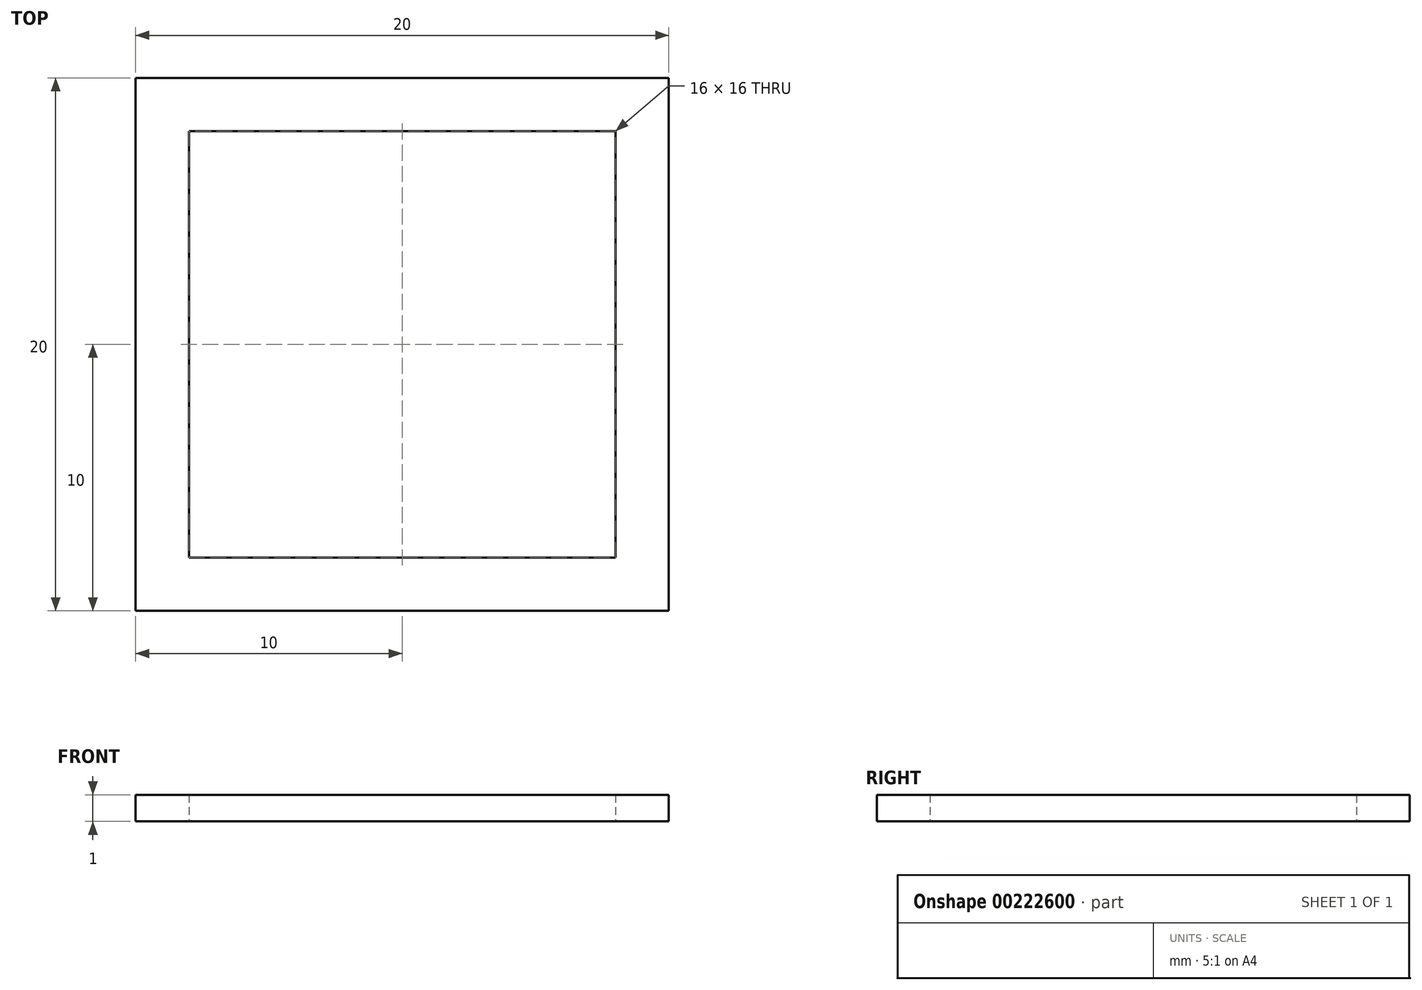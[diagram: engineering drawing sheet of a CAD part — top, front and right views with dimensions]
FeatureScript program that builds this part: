
annotation { "Feature Type Name" : "Feature", "Feature Type Description" : "" }
export const myFeature = defineFeature(function(context is Context, id is Id, definition is map)
    precondition{}
    {
        {
            var Q0;
            Q0=qCreatedBy(makeId("Top.planeOp"),FACE);
            var sketch = newSketch(context, id + "F0", { "sketchPlane" : qUnion([Q0])});
            skLineSegment(sketch, "E0.bottom", {"start": v(10, -10) * mm, "end": v(-10, -10) * mm});
            skLineSegment(sketch, "E0.top", {"start": v(10, 10) * mm, "end": v(-10, 10) * mm});
            skLineSegment(sketch, "E0.left", {"start": v(10, -10) * mm, "end": v(10, 10) * mm});
            skLineSegment(sketch, "E0.right", {"start": v(-10, -10) * mm, "end": v(-10, 10) * mm});
            skPoint(sketch, "E0.middle", {"position": v(0, 0) * mm});
            skLineSegment(sketch, "E1.bottom", {"start": v(8, -8) * mm, "end": v(-8, -8) * mm});
            skLineSegment(sketch, "E1.top", {"start": v(8, 8) * mm, "end": v(-8, 8) * mm});
            skLineSegment(sketch, "E1.left", {"start": v(8, -8) * mm, "end": v(8, 8) * mm});
            skLineSegment(sketch, "E1.right", {"start": v(-8, -8) * mm, "end": v(-8, 8) * mm});
            skSolve(sketch);
        }
        {
            var Q0;
            Q0=makeQuery(id+"F0.imprint","IMPRINT",FACE,{"disambiguationData":[TD([[makeQuery(id+"F0.imprint","IMPRINT",EDGE,{"derivedFrom":sQuery(id+"F0.wireOp",EDGE,"E0.bottom")}),-1.0]])]});
            extrude(context, id + "F1", {"entities" : qUnion([Q0]), "depth" : 1 * mm});
        }
    });
